# Revit family: HBA
name_source: partatom
category: Осветительные приборы
revit_build: Autodesk Revit 2016 (Build: 20150220_1215(x64)
units: mm (PartAtom-declared; Revit-internal decimal feet)

## family parameters
Источник света = Да
Общий = Нет
Основа = Грань
При загрузке вырезать с полостями = Нет
Размер круглого соединителя = Использовать диаметр
Тип детали = Нормальный
Точка расчета площади = Нет

## types (1)
- HBA
    ADSK_Единица измерения = Шт.
    ADSK_Завод-изготовитель = ООО МГК Световые технологии
    ADSK_Код изделия = 1311000030
    ADSK_Количество фаз = 1
    ADSK_Количество фаз числовое = 1
    ADSK_Коэффициент мощности = 0.85
    ADSK_Масса = 9
    ADSK_Наименование = Серия подвесных светильников для освещения промышленных предприятий с пластиковым корпусом, гладким отражателем и защитным стеклом. Имеет высокую степень защиты IP65 и высокий световой поток. Возможен заказ модификаций с IP23 без защитного стекла. Преимущества светильника: возможность безопасного изменения светового центра путем перемещения лампы вместе с патроном по вертикали, а также второй класcзащиты от поражения электрическим током. В качестве источника света используется газоразрядная лампа высокого давления до 400 Вт
    ADSK_Напряжение = 230 В
    ADSK_Номинальная мощность = 0 кВт
    ADSK_Полная мощность = 0 кВ·А
    ADSK_Размер_Высота = 590 мм
    ADSK_Размер_Ширина = 485 мм
    ADSK_Ток = 1 А
    ADSK_Энергоэффективность = 28 лм/Вт
    IP Class = IP65
    URL = https://ltcompany.com
    Блок аварийного питания = Нет
    Видимая форма излучения при визуализации = Нет
    Группа модели = Светильники
    Защитное стекло = Плафон прозрачный
    Изготовитель = ООО МГК Световые технологии
    Излучение по длине прямоугольника = 485 мм
    Излучение по ширине прямоугольника = 485 мм
    Класс Защиты = II
    Класс пожароопасности = П-I,II,IIа
    Климатическая зона = УХЛ2
    Код по классификатору = D5020200
    Корпус = Черный пластик
    Область использования = Промышленные предприятия, Складские объекты, Спортзалы, ТРЦ
    Описание = Серия подвесных светильников для освещения промышленных предприятий с пластиковым корпусом, гладким отражателем и защитным стеклом. Имеет высокую степень защиты IP65 и высокий световой поток. Возможен заказ модификаций с IP23 без защитного стекла. Преимущества светильника: возможность безопасного изменения светового центра путем перемещения лампы вместе с патроном по вертикали, а также второй класcзащиты от поражения электрическим током. В качестве источника света используется газоразрядная лампа высокого давления до 400 Вт
    Отметка по умолчанию = 0 мм
    Плафон = Белый пластик
    Полная установленная мощность = 0 кВ·А
    Разработчик = ООО ПРОРУБИМ
    Разработчик (телефон) = +7 (495) 649-85-43
    Решетка = Cерый металл
    Светофильтр = 16777215
    Смещение цветовой температуры при затухании лампы = <Нет>
    Тип ИС = МГЛ
    Тип ПРА = ЭмПРА
    Угол наклона = -90.00°
    Файл фотометрической сетки = generic
